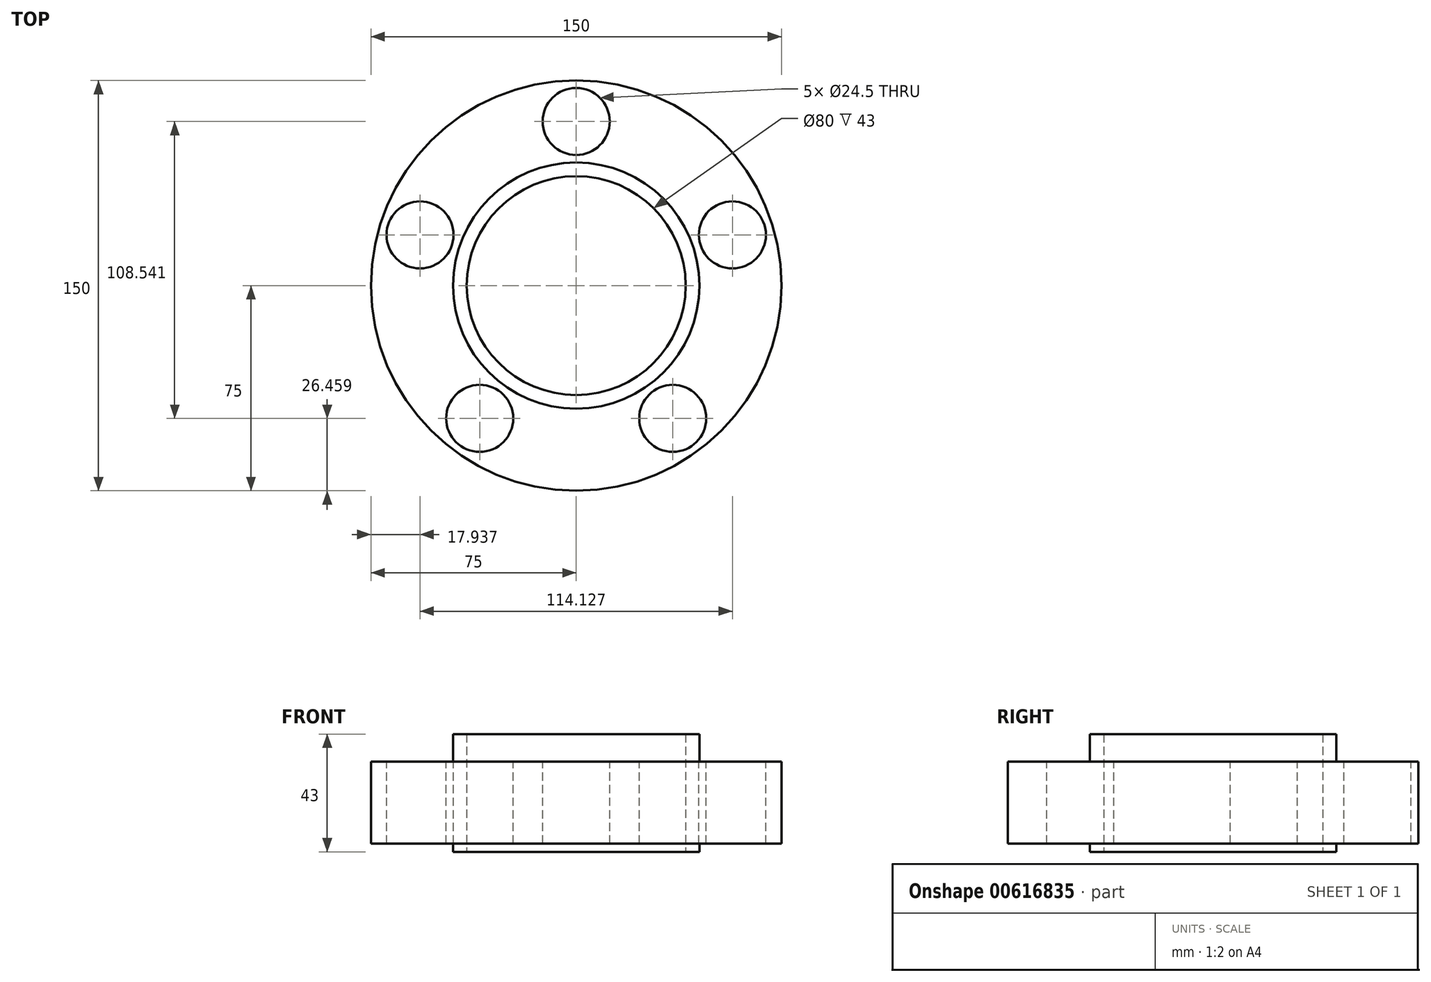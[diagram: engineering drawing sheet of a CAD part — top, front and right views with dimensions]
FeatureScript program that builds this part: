
annotation { "Feature Type Name" : "Feature", "Feature Type Description" : "" }
export const myFeature = defineFeature(function(context is Context, id is Id, definition is map)
    precondition{}
    {
        {
            var Q0;
            Q0=qCreatedBy(makeId("Front.planeOp"),FACE);
            var sketch = newSketch(context, id + "F0", { "sketchPlane" : qUnion([Q0])});
            skLineSegment(sketch, "E0", {"start": v(40, 0) * mm, "end": v(40, 43) * mm});
            skLineSegment(sketch, "E1", {"start": v(40, 43) * mm, "end": v(45, 43) * mm});
            skLineSegment(sketch, "E2", {"start": v(45, 43) * mm, "end": v(45, 33) * mm});
            skLineSegment(sketch, "E3", {"start": v(45, 33) * mm, "end": v(75, 33) * mm});
            skLineSegment(sketch, "E4", {"start": v(75, 33) * mm, "end": v(75, 3) * mm});
            skLineSegment(sketch, "E5", {"start": v(75, 3) * mm, "end": v(45, 3) * mm});
            skLineSegment(sketch, "E6", {"start": v(45, 3) * mm, "end": v(45, 0) * mm});
            skLineSegment(sketch, "E7", {"start": v(45, 0) * mm, "end": v(40, 0) * mm});
            skLineSegment(sketch, "E8", {"start": v(0, 0) * mm, "end": v(0, 79.57) * mm, "construction": true});
            skSolve(sketch);
        }
        {
            var Q0;
            Q0=makeQuery(id+"F0.imprint","IMPRINT",FACE,{"disambiguationData":[TD([[makeQuery(id+"F0.imprint","IMPRINT",EDGE,{"derivedFrom":sQuery(id+"F0.wireOp",EDGE,"E0")}),-1.0]])]});
            var Q1;
            Q1=sQuery(id+"F0.wireOp",EDGE,"E8");
            revolve(context, id + "F1", {"surfaceOperationType" : NewSurfaceOperationType.NEW, "entities" : qUnion([Q0]), "axis" : qUnion([Q1]), "revolveType" : RevolveType.FULL});
        }
        {
            var Q0;
            Q0=makeQuery(id+"F1.opRevolve","SWEPT_FACE",FACE,{"disambiguationData":[OSD([sQuery(id+"F0.wireOp",EDGE,"E3")])]});
            var sketch = newSketch(context, id + "F2", { "sketchPlane" : qUnion([Q0])});
            skCircle(sketch, "E9", {"center": v(0, 0) * mm, "radius": 60 * mm, "construction": true});
            skCircle(sketch, "E10", {"center": v(0, 60) * mm, "radius": 12.25 * mm});
            skCircle(sketch, "E11.1.0", {"center": v(-57.06, 18.54) * mm, "radius": 12.25 * mm});
            skCircle(sketch, "E11.2.0", {"center": v(-35.27, -48.54) * mm, "radius": 12.25 * mm});
            skCircle(sketch, "E11.3.0", {"center": v(35.27, -48.54) * mm, "radius": 12.25 * mm});
            skCircle(sketch, "E11.4.0", {"center": v(57.06, 18.54) * mm, "radius": 12.25 * mm});
            skLineSegment(sketch, "E12", {"start": v(0, 0) * mm, "end": v(-57.06, 18.54) * mm, "construction": true});
            skSolve(sketch);
        }
        {
            var Q0;
            Q0 = qSketchRegion(id + "F2", true);
            extrude(context, id + "F3", {"entities" : qUnion([Q0]), "operationType" : NewBodyOperationType.REMOVE, "endBound" : BoundingType.UP_TO_NEXT, "oppositeDirection" : true, "depth" : 25 * mm, "offsetDistance" : 25 * mm});
        }
    });
